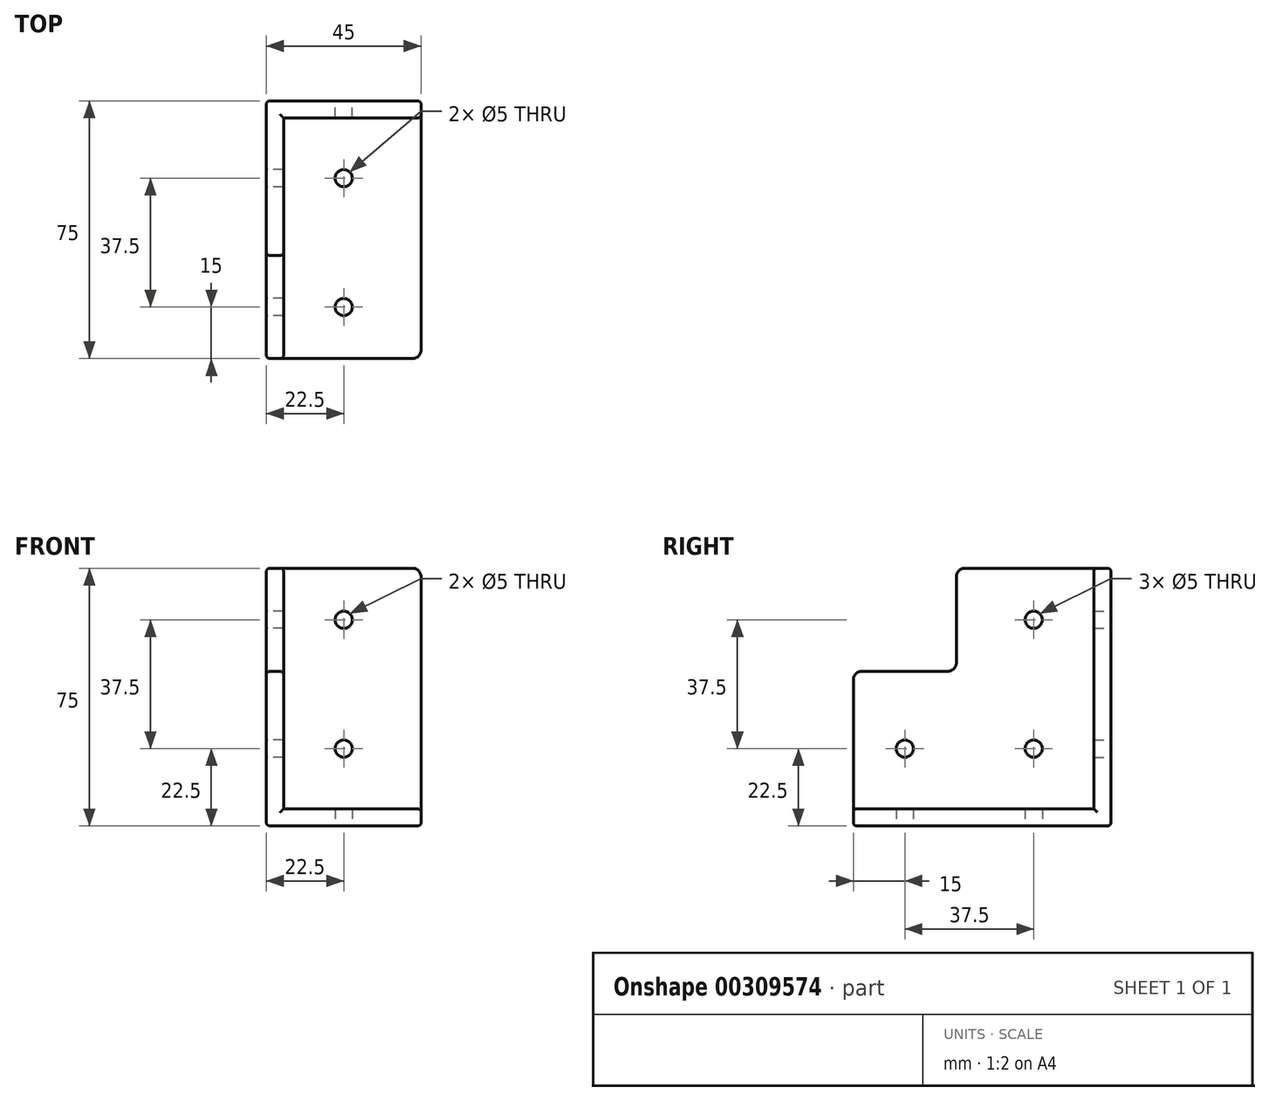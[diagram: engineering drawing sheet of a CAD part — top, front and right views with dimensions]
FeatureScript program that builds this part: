
annotation { "Feature Type Name" : "Feature", "Feature Type Description" : "" }
export const myFeature = defineFeature(function(context is Context, id is Id, definition is map)
    precondition{}
    {
        {
            var Q0;
            Q0=qCreatedBy(makeId("Top.planeOp"),FACE);
            var sketch = newSketch(context, id + "F0", { "sketchPlane" : qUnion([Q0])});
            skLineSegment(sketch, "E0.bottom", {"start": v(22.5, 22.5) * mm, "end": v(-22.5, 22.5) * mm});
            skLineSegment(sketch, "E0.top", {"start": v(22.5, -22.5) * mm, "end": v(-22.5, -22.5) * mm});
            skLineSegment(sketch, "E0.left", {"start": v(22.5, 22.5) * mm, "end": v(22.5, -22.5) * mm});
            skLineSegment(sketch, "E0.right", {"start": v(-22.5, 22.5) * mm, "end": v(-22.5, -22.5) * mm});
            skPoint(sketch, "E0.middle", {"position": v(0, 0) * mm});
            skSolve(sketch);
        }
        {
            var Q0;
            Q0=makeQuery(id+"F0.imprint","IMPRINT",FACE,{"disambiguationData":[TD([[makeQuery(id+"F0.imprint","IMPRINT",EDGE,{"derivedFrom":sQuery(id+"F0.wireOp",EDGE,"E0.bottom")}),1.0]])]});
            extrude(context, id + "F1", {"entities" : qUnion([Q0]), "depth" : 45 * mm, "offsetDistance" : 25 * mm});
        }
        {
            var Q0;
            Q0=makeQuery(id+"F1.opExtrude","CAP_FACE",FACE,{"disambiguationData":[OSD([sQuery(id+"F0.wireOp",EDGE,"E0.bottom"),sQuery(id+"F0.wireOp",EDGE,"E0.top"),sQuery(id+"F0.wireOp",EDGE,"E0.left"),sQuery(id+"F0.wireOp",EDGE,"E0.right")])],"isStart":false});
            var Q1;
            Q1=makeQuery(id+"F1.opExtrude","SWEPT_FACE",FACE,{"disambiguationData":[OSD([sQuery(id+"F0.wireOp",EDGE,"E0.left")])]});
            var Q2;
            Q2=makeQuery(id+"F1.opExtrude","SWEPT_FACE",FACE,{"disambiguationData":[OSD([sQuery(id+"F0.wireOp",EDGE,"E0.top")])]});
            shell(context, id + "F2", {"entities" : qUnion([Q0, Q1, Q2]), "thickness" : 5 * mm});
        }
        {
            var Q0;
            Q0=makeQuery(id+"F1.opExtrude","SWEPT_FACE",FACE,{"disambiguationData":[OSD([sQuery(id+"F0.wireOp",EDGE,"E0.top")])]});
            extrude(context, id + "F3", {"entities" : qUnion([Q0]), "depth" : 30 * mm, "offsetDistance" : 25 * mm});
        }
        {
            var Q0;
            Q0=makeQuery(id+"F1.opExtrude","CAP_FACE",FACE,{"disambiguationData":[OSD([sQuery(id+"F0.wireOp",EDGE,"E0.bottom"),sQuery(id+"F0.wireOp",EDGE,"E0.top"),sQuery(id+"F0.wireOp",EDGE,"E0.left"),sQuery(id+"F0.wireOp",EDGE,"E0.right")])],"isStart":false});
            extrude(context, id + "F4", {"entities" : qUnion([Q0]), "depth" : 30 * mm, "offsetDistance" : 25 * mm});
        }
        {
            var Q0;
            {var subQ0=sQuery(id+"F0.wireOp",EDGE,"E0.right");var subQ1=sQuery(id+"F0.wireOp",EDGE,"E0.top");Q0=makeQuery(id+"F3.opExtrude","SWEPT_FACE",FACE,{"disambiguationData":[OSD([subQ1,subQ0]),TDD([makeQuery(id+"F1.opExtrude","SWEPT_EDGE",EDGE,{"disambiguationData":[OSD([subQ1,subQ0])]})])]});}
            var sketch = newSketch(context, id + "F5", { "sketchPlane" : qUnion([Q0])});
            skPoint(sketch, "E1", {"position": v(37.5, 22.5) * mm});
            skPoint(sketch, "E1.positionSnap0", {"position": v(37.5, 0) * mm});
            skPoint(sketch, "E2", {"position": v(52.5, 22.5) * mm});
            skPoint(sketch, "E3", {"position": v(22.5, 22.5) * mm});
            skPoint(sketch, "E4", {"position": v(0, 0) * mm});
            skLineSegment(sketch, "E5", {"start": v(22.5, 22.5) * mm, "end": v(52.5, 22.5) * mm, "construction": true});
            skPoint(sketch, "E6", {"position": v(37.5, 45) * mm});
            skLineSegment(sketch, "E7", {"start": v(37.5, 0) * mm, "end": v(37.5, 45) * mm, "construction": true});
            skSolve(sketch);
        }
        {
            var Q0;
            {var subQ0=sQuery(id+"F0.wireOp",EDGE,"E0.right");Q0=makeQuery(id+"F4.opExtrude","SWEPT_FACE",FACE,{"disambiguationData":[OSD([subQ0]),TDD([makeQuery(id+"F1.opExtrude","CAP_EDGE",EDGE,{"disambiguationData":[OSD([subQ0])],"isStart":false})])]});}
            var sketch = newSketch(context, id + "F6", { "sketchPlane" : qUnion([Q0])});
            skPoint(sketch, "E8", {"position": v(-22.5, 60) * mm});
            skPoint(sketch, "E9", {"position": v(22.5, 60) * mm});
            skPoint(sketch, "E10", {"position": v(0, 75) * mm});
            skPoint(sketch, "E11", {"position": v(0, 45) * mm});
            skPoint(sketch, "E12", {"position": v(0, 60) * mm});
            skLineSegment(sketch, "E13", {"start": v(-22.5, 60) * mm, "end": v(22.5, 60) * mm, "construction": true});
            skLineSegment(sketch, "E14", {"start": v(0, 75) * mm, "end": v(0, 45) * mm, "construction": true});
            skSolve(sketch);
        }
        {
            var Q0;
            Q0=makeQuery(id+"F1.opExtrude","SWEPT_FACE",FACE,{"disambiguationData":[OSD([sQuery(id+"F0.wireOp",EDGE,"E0.right")])]});
            var sketch = newSketch(context, id + "F7", { "sketchPlane" : qUnion([Q0])});
            skPoint(sketch, "E15", {"position": v(-22.5, 22.5) * mm});
            skLineSegment(sketch, "E16", {"start": v(-22.5, 22.5) * mm, "end": v(22.5, 22.5) * mm, "construction": true});
            skLineSegment(sketch, "E17", {"start": v(0, 45) * mm, "end": v(0, 0) * mm, "construction": true});
            skPoint(sketch, "E18", {"position": v(0, 22.5) * mm});
            skSolve(sketch);
        }
        {
            var Q0;
            Q0=makeQuery(id+"F1.opExtrude","SWEPT_FACE",FACE,{"disambiguationData":[OSD([sQuery(id+"F0.wireOp",EDGE,"E0.bottom")])]});
            var sketch = newSketch(context, id + "F8", { "sketchPlane" : qUnion([Q0])});
            skPoint(sketch, "E19", {"position": v(0, 22.5) * mm});
            skPoint(sketch, "E19.positionSnap0", {"position": v(22.5, 22.5) * mm});
            skPoint(sketch, "E20.0", {"position": v(22.5, 60) * mm});
            skPoint(sketch, "E21", {"position": v(0, 60) * mm});
            skSolve(sketch);
        }
        {
            var Q0;
            Q0=makeQuery(id+"F1.opExtrude","CAP_FACE",FACE,{"disambiguationData":[OSD([sQuery(id+"F0.wireOp",EDGE,"E0.bottom"),sQuery(id+"F0.wireOp",EDGE,"E0.top"),sQuery(id+"F0.wireOp",EDGE,"E0.left"),sQuery(id+"F0.wireOp",EDGE,"E0.right")])],"isStart":true});
            var sketch = newSketch(context, id + "F9", { "sketchPlane" : qUnion([Q0])});
            skPoint(sketch, "E22", {"position": v(0, 0) * mm});
            skPoint(sketch, "E23.0", {"position": v(-22.5, 37.5) * mm});
            skPoint(sketch, "E24", {"position": v(0, 37.5) * mm});
            skSolve(sketch);
        }
        {
            var Q0;
            Q0=sQuery(id+"F8.wireOp",VERTEX,"E21");
            var Q1;
            Q1=sQuery(id+"F6.wireOp",VERTEX,"E12");
            var Q2;
            Q2=sQuery(id+"F7.wireOp",VERTEX,"E18");
            var Q3;
            Q3=sQuery(id+"F8.wireOp",VERTEX,"E19");
            var Q4;
            Q4=sQuery(id+"F9.wireOp",VERTEX,"E22");
            var Q5;
            Q5=sQuery(id+"F9.wireOp",VERTEX,"E24");
            var Q6;
            Q6=sQuery(id+"F5.wireOp",VERTEX,"E1");
            var Q7;
            Q7=makeQuery(id+"F4.opExtrude","SWEPT_BODY",BODY,{"disambiguationData":[OSD([sQuery(id+"F0.wireOp",EDGE,"E0.bottom"),sQuery(id+"F0.wireOp",EDGE,"E0.top"),sQuery(id+"F0.wireOp",EDGE,"E0.left"),sQuery(id+"F0.wireOp",EDGE,"E0.right")])]});
            var Q8;
            Q8=makeQuery(id+"F1.opExtrude","SWEPT_BODY",BODY,{"disambiguationData":[OSD([sQuery(id+"F0.wireOp",EDGE,"E0.bottom"),sQuery(id+"F0.wireOp",EDGE,"E0.top"),sQuery(id+"F0.wireOp",EDGE,"E0.left"),sQuery(id+"F0.wireOp",EDGE,"E0.right")])]});
            var Q9;
            Q9=makeQuery(id+"F3.opExtrude","SWEPT_BODY",BODY,{"disambiguationData":[OSD([sQuery(id+"F0.wireOp",EDGE,"E0.top")])]});
            hole(context, id + "F10", {"style" : HoleStyle.SIMPLE, "endStyle" : HoleEndStyle.THROUGH, "standardTappedOrClearance" : lookupTablePath({ "standard" : "ISO", "size" : "5", "type" : "Drilled" }), "standardBlindInLast" : lookupTablePath({ "standard" : "ISO", "size" : "5", "type" : "Drilled" }), "holeDiameter" : 5 * mm, "majorDiameter" : 5 * mm, "isTappedThrough" : true, "tappedDepth" : 12 * mm, "tapClearance" : 3, "startFromSketch" : true, "locations" : qUnion([Q0, Q1, Q2, Q3, Q4, Q5, Q6]), "scope" : qUnion([Q7, Q8, Q9])});
        }
        {
            var Q0;
            Q0=makeQuery(id+"F1.opExtrude","SWEPT_BODY",BODY,{"disambiguationData":[OSD([sQuery(id+"F0.wireOp",EDGE,"E0.bottom"),sQuery(id+"F0.wireOp",EDGE,"E0.top"),sQuery(id+"F0.wireOp",EDGE,"E0.left"),sQuery(id+"F0.wireOp",EDGE,"E0.right")])]});
            var Q1;
            Q1=makeQuery(id+"F3.opExtrude","SWEPT_BODY",BODY,{"disambiguationData":[OSD([sQuery(id+"F0.wireOp",EDGE,"E0.top")])]});
            var Q2;
            Q2=makeQuery(id+"F4.opExtrude","SWEPT_BODY",BODY,{"disambiguationData":[OSD([sQuery(id+"F0.wireOp",EDGE,"E0.bottom"),sQuery(id+"F0.wireOp",EDGE,"E0.top"),sQuery(id+"F0.wireOp",EDGE,"E0.left"),sQuery(id+"F0.wireOp",EDGE,"E0.right")])]});
            booleanBodies(context, id + "F11", {"operationType" : BooleanOperationType.UNION, "tools" : qUnion([Q0, Q1, Q2])});
        }
        {
            var Q0;
            Q0=makeQuery(id+"F4.opExtrude","CAP_EDGE",EDGE,{"disambiguationData":[OSD([sQuery(id+"F0.wireOp",EDGE,"E0.top")])],"isStart":true});
            var Q1;
            Q1=makeQuery(id+"F4.opExtrude","CAP_EDGE",EDGE,{"disambiguationData":[OSD([sQuery(id+"F0.wireOp",EDGE,"E0.top")])],"isStart":false});
            var Q2;
            {var subQ0=sQuery(id+"F0.wireOp",EDGE,"E0.top");Q2=makeQuery(id+"F3.opExtrude","CAP_EDGE",EDGE,{"disambiguationData":[OSD([subQ0]),TDD([makeQuery(id+"F1.opExtrude","CAP_EDGE",EDGE,{"disambiguationData":[OSD([subQ0])],"isStart":false})])],"isStart":false});}
            var Q3;
            Q3=makeQuery(id+"F4.opExtrude","CAP_EDGE",EDGE,{"disambiguationData":[OSD([sQuery(id+"F0.wireOp",EDGE,"E0.left")])],"isStart":false});
            var Q4;
            Q4=makeQuery(id+"F3.opExtrude","CAP_EDGE",EDGE,{"disambiguationData":[OSD([sQuery(id+"F0.wireOp",EDGE,"E0.top"),sQuery(id+"F0.wireOp",EDGE,"E0.left")])],"isStart":false});
            fillet(context, id + "F12", {"entities" : qUnion([Q0, Q1, Q2, Q3, Q4]), "radius" : 2.5 * mm, "tangentPropagation" : true, "allowEdgeOverflow" : false});
        }
        {
            var Q0;
            {var subQ0=sQuery(id+"F0.wireOp",EDGE,"E0.bottom");Q0=makeQuery(id+"F4.opExtrude","CAP_EDGE",EDGE,{"disambiguationData":[OSD([subQ0]),TDD([makeQuery(id+"F2.opShell","OFFSET_EDGE",EDGE,{"disambiguationData":[OSD([subQ0]),TDD([makeQuery(id+"F1.opExtrude","CAP_EDGE",EDGE,{"disambiguationData":[OSD([subQ0])],"isStart":false})])]})])],"isStart":false});}
            var Q1;
            {var subQ0=sQuery(id+"F0.wireOp",EDGE,"E0.right");Q1=makeQuery(id+"F4.opExtrude","CAP_EDGE",EDGE,{"disambiguationData":[OSD([subQ0]),TDD([makeQuery(id+"F2.opShell","OFFSET_EDGE",EDGE,{"disambiguationData":[OSD([subQ0]),TDD([makeQuery(id+"F1.opExtrude","CAP_EDGE",EDGE,{"disambiguationData":[OSD([subQ0])],"isStart":false})])]})])],"isStart":false});}
            var Q2;
            {var subQ0=sQuery(id+"F0.wireOp",EDGE,"E0.top");Q2=makeQuery(id+"F3.opExtrude","CAP_EDGE",EDGE,{"disambiguationData":[OSD([subQ0]),TDD([makeQuery(id+"F2.opShell","OFFSET_EDGE",EDGE,{"disambiguationData":[OSD([subQ0])]})])],"isStart":false});}
            var Q3;
            {var subQ0=sQuery(id+"F0.wireOp",EDGE,"E0.bottom");Q3=makeQuery(id+"F4.opExtrude","CAP_EDGE",EDGE,{"disambiguationData":[OSD([subQ0]),TDD([makeQuery(id+"F1.opExtrude","CAP_EDGE",EDGE,{"disambiguationData":[OSD([subQ0])],"isStart":false})])],"isStart":false});}
            var Q4;
            {var subQ0=sQuery(id+"F0.wireOp",EDGE,"E0.left");var subQ1=sQuery(id+"F0.wireOp",EDGE,"E0.top");Q4=makeQuery(id+"F11.opBoolean","MERGE",EDGE,{"derivedFrom":[makeQuery(id+"F1.opExtrude","CAP_EDGE",EDGE,{"disambiguationData":[OSD([subQ0])],"isStart":true}),makeQuery(id+"F3.opExtrude","SWEPT_EDGE",EDGE,{"disambiguationData":[OSD([subQ1,subQ0]),TDD([makeQuery(id+"F1.opExtrude","CAP_VERTEX",VERTEX,{"disambiguationData":[OSD([subQ1,subQ0])],"isStart":true})])]})]});}
            var Q5;
            Q5=makeQuery(id+"F1.opExtrude","CAP_EDGE",EDGE,{"disambiguationData":[OSD([sQuery(id+"F0.wireOp",EDGE,"E0.bottom")])],"isStart":true});
            var Q6;
            {var subQ0=sQuery(id+"F0.wireOp",EDGE,"E0.right");Q6=makeQuery(id+"F4.opExtrude","CAP_EDGE",EDGE,{"disambiguationData":[OSD([subQ0]),TDD([makeQuery(id+"F1.opExtrude","CAP_EDGE",EDGE,{"disambiguationData":[OSD([subQ0])],"isStart":false})])],"isStart":false});}
            var Q7;
            {var subQ0=sQuery(id+"F0.wireOp",EDGE,"E0.right");var subQ1=sQuery(id+"F0.wireOp",EDGE,"E0.bottom");Q7=makeQuery(id+"F11.opBoolean","MERGE",EDGE,{"derivedFrom":[makeQuery(id+"F1.opExtrude","SWEPT_EDGE",EDGE,{"disambiguationData":[OSD([subQ1,subQ0])]}),makeQuery(id+"F4.opExtrude","SWEPT_EDGE",EDGE,{"disambiguationData":[OSD([subQ1,subQ0]),TDD([makeQuery(id+"F1.opExtrude","CAP_VERTEX",VERTEX,{"disambiguationData":[OSD([subQ1,subQ0])],"isStart":false})])]})]});}
            var Q8;
            {var subQ0=sQuery(id+"F0.wireOp",EDGE,"E0.right");var subQ1=sQuery(id+"F0.wireOp",EDGE,"E0.top");Q8=makeQuery(id+"F11.opBoolean","MERGE",EDGE,{"derivedFrom":[makeQuery(id+"F1.opExtrude","CAP_EDGE",EDGE,{"disambiguationData":[OSD([subQ0])],"isStart":true}),makeQuery(id+"F3.opExtrude","SWEPT_EDGE",EDGE,{"disambiguationData":[OSD([subQ1,subQ0]),TDD([makeQuery(id+"F1.opExtrude","CAP_VERTEX",VERTEX,{"disambiguationData":[OSD([subQ1,subQ0])],"isStart":true})])]})]});}
            fillet(context, id + "F13", {"entities" : qUnion([Q0, Q1, Q2, Q3, Q4, Q5, Q6, Q7, Q8]), "radius" : 1 * mm, "tangentPropagation" : true, "allowEdgeOverflow" : false});
        }
    });
